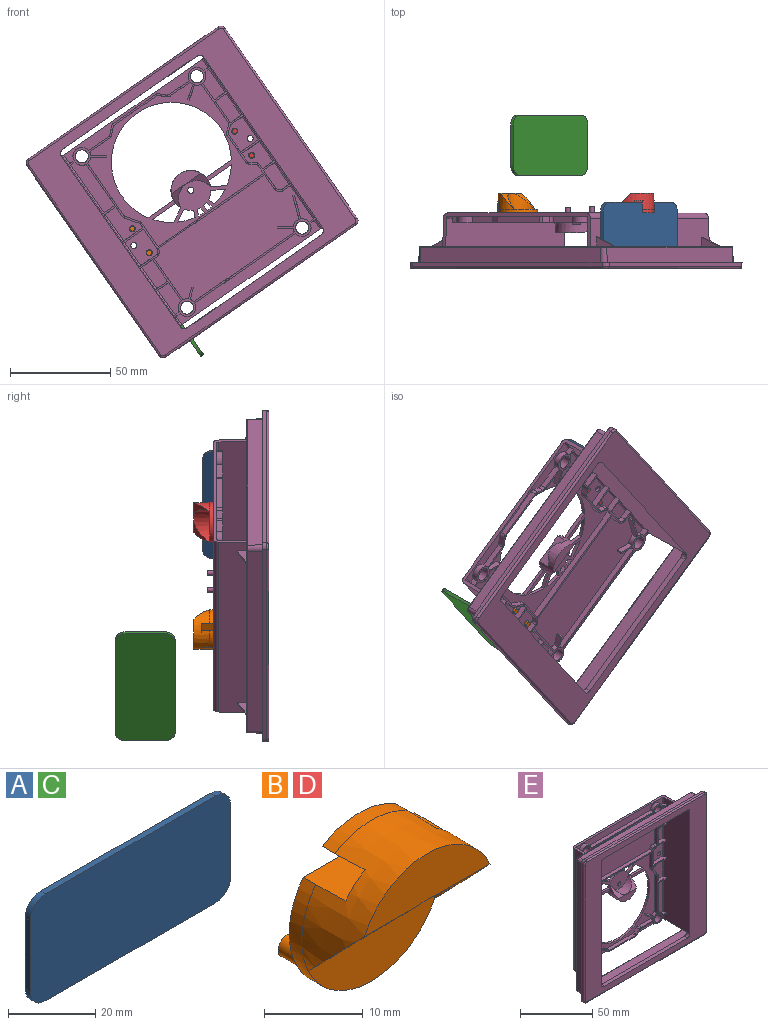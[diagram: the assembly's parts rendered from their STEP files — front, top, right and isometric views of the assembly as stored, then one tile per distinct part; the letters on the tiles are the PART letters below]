
ASSEMBLY  parts=5 mates=5
PART A: 10 faces, bbox 65x1.6x30 mm
  f0: plane 20x1.6mm, normal (1,0,0), area 32mm2, adj f1,f7,f8,f9
  f1: cylinder r=5mm len=5mm, axis (0,1,0), area 12.6mm2, adj f0,f2,f8,f9
  f2: plane 55x1.6mm, normal (0,0,1), area 88mm2, adj f1,f3,f8,f9
  f3: cylinder r=5mm len=5mm, axis (0,1,0), area 12.6mm2, adj f2,f4,f8,f9
  f4: plane 20x1.6mm, normal (-1,0,0), area 32mm2, adj f3,f5,f8,f9
  f5: cylinder r=5mm len=5mm, axis (0,1,0), area 12.6mm2, adj f4,f6,f8,f9
  f6: plane 55x1.6mm, normal (0,0,-1), area 88mm2, adj f5,f7,f8,f9
  f7: cylinder r=5mm len=5mm, axis (0,1,0), area 12.6mm2, adj f0,f6,f8,f9
  f8: plane 65x30mm, normal (0,-1,0), area 1928.5mm2, adj f0,f1,f2,f3,f4,f5,f6,f7
  f9: plane 65x30mm, normal (0,1,0), area 1928.5mm2, adj f0,f1,f2,f3,f4,f5,f6,f7
PART B: 18 faces, bbox 20x12.8x20 mm
  f0: plane 20x16mm, normal (0,1,0), area 252.1mm2, adj f4,f6,f7,f9,f14
  f1: plane 10.54x1.5mm, normal (0,1,0), area 10.7mm2, adj f5,f13
  f2: cone r=10mm half-angle=1deg, axis (0,1,0), area 219.9mm2, adj f4,f5,f12,f13,f14,f15,f16,f17
  f3: plane 18.1x14mm, normal (0,-1,0), area 181.7mm2, adj f4,f6,f11
  f4: cylinder r=10mm len=20mm, axis (0,-1,0), area 79.7mm2, adj f0,f2,f3,f14
  f5: cylinder r=10mm len=10.54mm, axis (0,-1,0), area 20mm2, adj f1,f2,f13
  f6: cylinder r=1.55mm len=3.1mm, axis (0,-1,0), area 17.5mm2, adj f0,f3
  f7: cylinder r=1.25mm len=3mm, axis (0,-1,0), area 23.6mm2, adj f0,f8
  f8: plane 2.5x2.5mm, normal (0,1,0), area 4.9mm2, adj f7
  f9: cylinder r=1.25mm len=3mm, axis (0,-1,0), area 23.6mm2, adj f0,f10
  f10: plane 2.5x2.5mm, normal (0,1,0), area 4.9mm2, adj f9
  f11: cone r=9.09mm half-angle=1deg, axis (0,-1,0), area 139.7mm2, adj f3,f12,f16,f17
  f12: plane 17.99x5.83mm, normal (0,-1,0), area 75.2mm2, adj f2,f11,f16,f17
  f13: plane 10.54x6mm, normal (0,0,-1), area 62.6mm2, adj f1,f2,f5,f15
  f14: plane 16x6mm, normal (0,0,1), area 95.6mm2, adj f0,f2,f4,f15
  f15: plane 15.82x2.5mm, normal (0,1,0), area 33.5mm2, adj f2,f13,f14
  f16: plane 8.54x8.28mm, normal (0,-0.72,-0.69), area 29.8mm2, adj f2,f11,f12
  f17: plane 8.54x8.28mm, normal (0,-0.72,-0.69), area 29.8mm2, adj f2,f11,f12
PART C: same geometry as A
PART D: same geometry as B
PART E: 328 faces, bbox 124.3x34.2x124.3 mm
  f0: cylinder r=30mm len=8.39mm, axis (0,-1,0), area 16.1mm2, adj f97,f100,f298,f317
  f1: cylinder r=30mm len=3.26mm, axis (0,-1,0), area 5.9mm2, adj f97,f100,f299,f301
  f2: cylinder r=30mm len=3.26mm, axis (0,-1,0), area 5.9mm2, adj f97,f100,f302,f304
  f3: cylinder r=30mm len=8.39mm, axis (0,-1,0), area 16.1mm2, adj f97,f100,f305,f307
  f4: cylinder r=30mm len=7.85mm, axis (0,-1,0), area 19.4mm2, adj f97,f100,f308,f310
  f5: cylinder r=30mm len=60mm, axis (0,-1,0), area 230.4mm2, adj f97,f100,f311,f312
  f6: cylinder r=30mm len=7.85mm, axis (0,-1,0), area 19.4mm2, adj f97,f100,f313,f315
  f7: plane 68x2.3mm, normal (0,1,0), area 156.4mm2, adj f16,f227,f239,f240
  f8: plane 21.25x2.3mm, normal (0,1,0), area 48.9mm2, adj f9,f16,f237,f238
  f9: plane 12.94x10.62mm, normal (0,0.01,-1), area 98.4mm2, adj f8,f16,f18,f230,f237,f241,f242,f281
  f10: plane 90.76x6.61mm, normal (0,1,0), area 599mm2, adj f13,f19,f224,f235,f285,f291
  f11: plane 68x2.3mm, normal (0,1,0), area 156.4mm2, adj f12,f224,f233,f234
  f12: plane 104x22.15mm, normal (1,0.02,0), area 2259.9mm2, adj f11,f13,f15,f20,f61,f99,f102,f103
  f13: plane 12.94x10.62mm, normal (0,0.01,1), area 98.4mm2, adj f10,f12,f20,f222,f231,f235,f236,f291
  f14: plane 7.72x7.51mm, normal (1,0.02,0), area 57.6mm2, adj f15,f87,f274,f283
  f15: plane 111.01x8.88mm, normal (0,1,0), area 303.6mm2, adj f12,f14,f16,f72,f73,f74,f86,f87
  f16: plane 104x22.15mm, normal (-1,0.02,0), area 2259.9mm2, adj f7,f8,f9,f15,f61,f101,f102,f103
  f17: plane 89.95x7.51mm, normal (1,0.02,0), area 674.8mm2, adj f18,f275,f279,f281
  f18: plane 90.76x6.61mm, normal (0,1,0), area 599mm2, adj f9,f17,f227,f241,f279,f281
  f19: plane 89.95x7.51mm, normal (-1,0.02,0), area 674.8mm2, adj f10,f276,f285,f291
  f20: plane 21.25x2.3mm, normal (0,1,0), area 48.9mm2, adj f12,f13,f231,f232
  f21: plane 7.72x7.51mm, normal (-1,0.02,0), area 57.6mm2, adj f61,f91,f266,f289
  f22: cone r=4.45mm half-angle=0.5deg, axis (0,1,0), area 10.2mm2, adj f97,f109,f148,f200
  f23: cone r=4.45mm half-angle=0.5deg, axis (0,1,0), area 10.2mm2, adj f97,f109,f146,f161
  f24: plane 104.01x25.12mm, normal (-1,-0.02,0), area 2592mm2, adj f25,f26,f27,f28,f55,f57,f63,f72
  f25: cylinder r=0.9mm len=15.12mm, axis (0,0,-1), area 21.1mm2, adj f24,f36,f140,f164
  f26: cylinder r=0.9mm len=13.12mm, axis (0,0,-1), area 18.3mm2, adj f24,f37,f163,f166
  f27: cylinder r=0.9mm len=14.12mm, axis (0,0,-1), area 19.7mm2, adj f24,f38,f167,f170
  f28: cylinder r=0.9mm len=16.12mm, axis (0,0,-1), area 22.5mm2, adj f24,f43,f169,f189
  f29: cylinder r=0.9mm len=13.12mm, axis (0,0,-1), area 18.3mm2, adj f41,f75,f191,f196
  f30: cylinder r=0.9mm len=14.12mm, axis (0,0,-1), area 19.7mm2, adj f42,f75,f190,f194
  f31: cylinder r=0.9mm len=14.12mm, axis (0,0,-1), area 19.7mm2, adj f40,f75,f144,f197
  f32: cylinder r=0.9mm len=12.12mm, axis (0,0,-1), area 16.9mm2, adj f44,f75,f193,f216
  f33: cylinder r=0.9mm len=13.12mm, axis (0,0,-1), area 18.3mm2, adj f34,f75,f215,f218
  f34: plane 13.1x6.56mm, normal (0,-1,0), area 84.6mm2, adj f33,f156,f215,f218,f219
  f35: plane 76.56x31.95mm, normal (0,-1,0), area 2286.4mm2, adj f45,f46,f58,f59,f60,f108,f131,f132
  f36: plane 15.1x6.56mm, normal (0,-1,0), area 87.3mm2, adj f25,f110,f140,f164,f186
  f37: plane 13.1x6.56mm, normal (0,-1,0), area 86mm2, adj f26,f163,f165,f166
  f38: plane 14.1x11.65mm, normal (0,-1,0), area 147.9mm2, adj f27,f167,f170,f175,f182,f184,f243,f248
  f39: plane 29.1x6.56mm, normal (0,-1,0), area 179.2mm2, adj f51,f55,f141,f160,f188
  f40: plane 14.1x6.56mm, normal (0,-1,0), area 80.8mm2, adj f31,f50,f144,f197,f199
  f41: plane 13.1x6.62mm, normal (0,-1,0), area 86mm2, adj f29,f191,f196,f198,f202
  f42: plane 14.1x10.61mm, normal (0,-1,0), area 129.9mm2, adj f30,f190,f192,f194,f204,f205,f213,f245
  f43: plane 16.1x11.65mm, normal (0,-1,0), area 129.4mm2, adj f28,f162,f169,f171,f176,f178,f181,f189
  f44: plane 12.1x10.61mm, normal (0,-1,0), area 100.4mm2, adj f32,f159,f193,f195,f207,f209,f212,f216
  f45: cone r=4.45mm half-angle=0.5deg, axis (0,1,0), area 9mm2, adj f35,f109,f153,f187
  f46: cone r=4.45mm half-angle=0.5deg, axis (0,1,0), area 6.7mm2, adj f35,f109,f152,f154
  f47: plane 84.02x5.15mm, normal (0,-1,0), area 378.4mm2, adj f48,f49,f57,f96,f102,f138,f139,f151
  f48: cone r=4.45mm half-angle=0.5deg, axis (0,1,0), area 39.2mm2, adj f47,f109,f138,f151
  f49: cone r=4.45mm half-angle=0.5deg, axis (0,1,0), area 39.2mm2, adj f47,f109,f139,f151
  f50: cone r=4.45mm half-angle=0.5deg, axis (0,1,0), area 18.3mm2, adj f40,f109,f144,f199
  f51: cone r=4.45mm half-angle=0.5deg, axis (0,1,0), area 18.3mm2, adj f39,f109,f141,f160
  f52: plane 84.02x5.15mm, normal (0,-1,0), area 252.6mm2, adj f53,f54,f98,f103,f111,f113,f116,f118
  f53: cylinder r=0.9mm len=5.17mm, axis (0,0,-1), area 7.2mm2, adj f52,f75,f103,f143
  f54: cone r=4.45mm half-angle=0.5deg, axis (0,1,0), area 39.2mm2, adj f52,f109,f116,f143
  f55: cylinder r=0.9mm len=29.12mm, axis (0,0,-1), area 40.7mm2, adj f24,f39,f141,f188
  f56: cone r=4.45mm half-angle=0.5deg, axis (0,1,0), area 5.5mm2, adj f97,f109,f114,f145
  f57: cylinder r=0.9mm len=5.17mm, axis (0,0,-1), area 7.2mm2, adj f24,f47,f102,f139
  f58: cylinder r=0.9mm len=20.12mm, axis (0,0,-1), area 28.1mm2, adj f35,f75,f137,f217
  f59: cone r=4.45mm half-angle=0.5deg, axis (0,1,0), area 13.6mm2, adj f35,f109,f135,f137
  f60: cone r=4.45mm half-angle=0.5deg, axis (0,1,0), area 14.8mm2, adj f35,f109,f132,f134
  f61: plane 111.01x8.88mm, normal (0,1,0), area 303.6mm2, adj f12,f16,f21,f76,f77,f78,f88,f89
  f62: plane 120.5x120.5mm, normal (0,1,0), area 1523.2mm2, adj f64,f65,f66,f67,f68,f69,f70,f71
  f63: plane 118.5x118.5mm, normal (0,-1,0), area 4621.4mm2, adj f24,f72,f73,f74,f75,f76,f77,f78
  f64: plane 115.5x2mm, normal (1,0,0), area 231mm2, adj f62,f65,f71,f252
  f65: cylinder r=2.5mm len=2.5mm, axis (0,-1,0), area 7.9mm2, adj f62,f64,f66,f254
  f66: plane 115.5x2mm, normal (0,0,1), area 231mm2, adj f62,f65,f67,f256
  f67: cylinder r=2.5mm len=2.5mm, axis (0,-1,0), area 7.9mm2, adj f62,f66,f68,f255
  f68: plane 115.5x2mm, normal (-1,0,0), area 231mm2, adj f62,f67,f69,f253
  f69: cylinder r=2.5mm len=2.5mm, axis (0,-1,0), area 7.9mm2, adj f62,f68,f70,f251
  f70: plane 115.5x2mm, normal (0,0,-1), area 231mm2, adj f62,f69,f71,f249
  f71: cylinder r=2.5mm len=2.5mm, axis (0,-1,0), area 7.9mm2, adj f62,f64,f70,f250
  f72: cone r=2.5mm half-angle=1deg, axis (0,-1,0), area 11.7mm2, adj f15,f24,f63,f73
  f73: plane 81.7x3mm, normal (0,-0.02,-1), area 245.1mm2, adj f15,f63,f72,f74
  f74: cone r=2.5mm half-angle=1deg, axis (0,-1,0), area 11.7mm2, adj f15,f63,f73,f75
  f75: plane 104.01x25.12mm, normal (1,-0.02,0), area 2590.1mm2, adj f29,f30,f31,f32,f33,f53,f58,f63
  f76: cone r=2.5mm half-angle=1deg, axis (0,-1,0), area 11.7mm2, adj f61,f63,f75,f77
  f77: plane 81.7x3mm, normal (0,-0.02,1), area 245.1mm2, adj f61,f63,f76,f78
  f78: cone r=2.5mm half-angle=1deg, axis (0,-1,0), area 11.7mm2, adj f24,f61,f63,f77
  f79: plane 109.5x7.51mm, normal (0,0.02,-1), area 822.3mm2, adj f62,f80,f94,f264
  f80: cone r=2.25mm half-angle=1deg, axis (0,-1,0), area 25.8mm2, adj f62,f79,f81,f262
  f81: plane 109.5x7.51mm, normal (-1,0.02,0), area 822.3mm2, adj f62,f80,f82,f260
  f82: cone r=2.25mm half-angle=1deg, axis (0,-1,0), area 25.8mm2, adj f62,f81,f83,f258
  f83: plane 109.5x7.51mm, normal (0,0.02,1), area 822.3mm2, adj f62,f82,f84,f257
  f84: cone r=2.25mm half-angle=1deg, axis (0,-1,0), area 25.8mm2, adj f62,f83,f85,f259
  f85: plane 109.5x7.51mm, normal (1,0.02,0), area 822.3mm2, adj f62,f84,f94,f261
  f86: plane 109.5x7.51mm, normal (0,0.02,-1), area 822.3mm2, adj f15,f87,f93,f272
  f87: cone r=0.75mm half-angle=1deg, axis (0,1,0), area 9.6mm2, adj f14,f15,f86,f273
  f88: plane 7.72x7.51mm, normal (1,0.02,0), area 57.6mm2, adj f61,f89,f265,f277
  f89: cone r=0.75mm half-angle=1deg, axis (0,1,0), area 9.6mm2, adj f61,f88,f90,f267
  f90: plane 109.5x7.51mm, normal (0,0.02,1), area 822.3mm2, adj f61,f89,f91,f269
  f91: cone r=0.75mm half-angle=1deg, axis (0,1,0), area 9.6mm2, adj f21,f61,f90,f268
  f92: plane 7.72x7.51mm, normal (-1,0.02,0), area 57.6mm2, adj f15,f93,f270,f287
  f93: cone r=0.75mm half-angle=1deg, axis (0,1,0), area 9.6mm2, adj f15,f86,f92,f271
  f94: cone r=2.25mm half-angle=1deg, axis (0,-1,0), area 25.8mm2, adj f62,f79,f85,f263
  f95: plane 112.79x112.79mm, normal (0,1,0), area 109.6mm2, adj f222,f225,f228,f230,f257,f258,f259,f260
  f96: cylinder r=0.9mm len=5.17mm, axis (0,0,-1), area 7.2mm2, adj f47,f75,f102,f138
  f97: plane 69.1x62.25mm, normal (0,-1,0), area 1388.1mm2, adj f0,f1,f2,f3,f4,f5,f6,f22
  f98: cylinder r=0.9mm len=5.17mm, axis (0,0,-1), area 7.2mm2, adj f24,f52,f103,f142
  f99: cylinder r=2.7mm len=103.23mm, axis (0,0,-1), area 432.7mm2, adj f12,f100,f102,f103
  f100: plane 103.13x84.02mm, normal (0,1,0), area 6018.9mm2, adj f0,f1,f2,f3,f4,f5,f6,f99
  f101: cylinder r=2.7mm len=103.23mm, axis (0,0,-1), area 432.7mm2, adj f16,f100,f102,f103
  f102: plane 90.22x24.82mm, normal (0,0.02,1), area 241.1mm2, adj f12,f15,f16,f24,f47,f57,f75,f96
  f103: plane 90.22x24.82mm, normal (0,0.02,-1), area 241mm2, adj f12,f16,f24,f52,f53,f61,f75,f98
  f104: cylinder r=3.25mm len=6.5mm, axis (0,-1,0), area 98mm2, adj f100,f109
  f105: cylinder r=3.25mm len=6.5mm, axis (0,-1,0), area 98mm2, adj f100,f109
  f106: cylinder r=3.25mm len=6.5mm, axis (0,-1,0), area 98mm2, adj f100,f109
  f107: cylinder r=3.25mm len=6.5mm, axis (0,-1,0), area 98mm2, adj f100,f109
  f108: cone r=4.45mm half-angle=0.5deg, axis (0,1,0), area 5.5mm2, adj f35,f109,f131,f152
  f109: plane 100.85x85.9mm, normal (0,-1,0), area 520.3mm2, adj f22,f23,f24,f45,f46,f48,f49,f50
  f110: cone r=4.45mm half-angle=0.5deg, axis (0,1,0), area 18.3mm2, adj f36,f109,f140,f186
  f111: cone r=4.45mm half-angle=0.5deg, axis (0,1,0), area 39.2mm2, adj f52,f109,f113,f142
  f112: cone r=4.45mm half-angle=0.5deg, axis (0,1,0), area 5.5mm2, adj f97,f109,f115,f149
  f113: plane 12.22x3mm, normal (0,-0.01,-1), area 36.6mm2, adj f52,f109,f111,f125
  f114: plane 12.22x3mm, normal (0,-0.01,1), area 36.6mm2, adj f56,f97,f109,f126
  f115: plane 11.8x3mm, normal (0,-0.01,1), area 35.4mm2, adj f97,f109,f112,f130
  f116: plane 11.8x3mm, normal (0,-0.01,-1), area 35.4mm2, adj f52,f54,f109,f129
  f117: plane 3x2.55mm, normal (0.71,-0.01,0.71), area 10.8mm2, adj f97,f109,f127,f130
  f118: plane 3x2.55mm, normal (-0.71,-0.01,-0.71), area 10.8mm2, adj f52,f109,f128,f129
  f119: plane 25.44x3mm, normal (0,-0.01,1), area 76.3mm2, adj f97,f109,f123,f127
  f120: plane 25.44x3mm, normal (0,-0.01,-1), area 76.3mm2, adj f52,f109,f124,f128
  f121: plane 3x2.85mm, normal (-0.71,-0.01,0.71), area 12mm2, adj f97,f109,f123,f126
  f122: plane 3x2.85mm, normal (0.71,-0.01,-0.71), area 12mm2, adj f52,f109,f124,f125
  f123: cone r=1.55mm half-angle=0.5deg, axis (0,-1,0), area 3.7mm2, adj f97,f109,f119,f121
  f124: cone r=2.45mm half-angle=0.5deg, axis (0,1,0), area 5.7mm2, adj f52,f109,f120,f122
  f125: cone r=1.55mm half-angle=0.5deg, axis (0,-1,0), area 3.7mm2, adj f52,f109,f113,f122
  f126: cone r=2.45mm half-angle=0.5deg, axis (0,1,0), area 5.7mm2, adj f97,f109,f114,f121
  f127: cone r=1.55mm half-angle=0.5deg, axis (0,-1,0), area 3.7mm2, adj f97,f109,f117,f119
  f128: cone r=2.45mm half-angle=0.5deg, axis (0,1,0), area 5.7mm2, adj f52,f109,f118,f120
  f129: cone r=2.55mm half-angle=0.5deg, axis (0,-1,0), area 6mm2, adj f52,f109,f116,f118
  f130: cone r=3.45mm half-angle=0.5deg, axis (0,1,0), area 8.1mm2, adj f97,f109,f115,f117
  f131: plane 6.61x4.61mm, normal (0.57,-0.01,0.82), area 24.1mm2, adj f35,f108,f109,f133
  f132: plane 6.58x4.64mm, normal (-0.57,-0.01,-0.82), area 24.1mm2, adj f35,f60,f109,f133
  f133: plane 3x0.74mm, normal (0.82,-0.01,-0.57), area 2.6mm2, adj f35,f109,f131,f132
  f134: plane 11.33x4.13mm, normal (0.94,-0.01,-0.34), area 36.1mm2, adj f35,f60,f109,f136
  f135: plane 11.31x4.14mm, normal (-0.94,-0.01,0.34), area 36.1mm2, adj f35,f59,f109,f136
  f136: plane 3x0.85mm, normal (-0.34,-0.01,-0.94), area 2.6mm2, adj f35,f109,f134,f135
  f137: plane 3.55x3mm, normal (0,-0.01,-1), area 10.4mm2, adj f35,f58,f59,f75,f109
  f138: plane 3.55x3mm, normal (0,-0.01,1), area 10.4mm2, adj f47,f48,f75,f96,f109
  f139: plane 3.55x3mm, normal (0,-0.01,1), area 10.4mm2, adj f24,f47,f49,f57,f109
  f140: plane 3.55x3mm, normal (0,-0.01,-1), area 10.4mm2, adj f24,f25,f36,f109,f110
  f141: plane 3.55x3mm, normal (0,-0.01,1), area 10.4mm2, adj f24,f39,f51,f55,f109
  f142: plane 3.55x3mm, normal (0,-0.01,-1), area 10.4mm2, adj f24,f52,f98,f109,f111
  f143: plane 3.55x3mm, normal (0,-0.01,-1), area 10.4mm2, adj f52,f53,f54,f75,f109
  f144: plane 3.55x3mm, normal (0,-0.01,1), area 10.4mm2, adj f31,f40,f50,f75,f109
  f145: plane 6.61x4.61mm, normal (-0.57,-0.01,-0.82), area 24.1mm2, adj f56,f97,f109,f147
  f146: plane 6.58x4.64mm, normal (0.57,-0.01,0.82), area 24.1mm2, adj f23,f97,f109,f147
  f147: plane 3x0.74mm, normal (-0.82,-0.01,0.57), area 2.6mm2, adj f97,f109,f145,f146
  f148: plane 6.58x4.64mm, normal (-0.57,-0.01,0.82), area 24.1mm2, adj f22,f97,f109,f150
  f149: plane 6.61x4.61mm, normal (0.57,-0.01,-0.82), area 24.1mm2, adj f97,f109,f112,f150
  f150: plane 3x0.74mm, normal (0.82,-0.01,0.57), area 2.6mm2, adj f97,f109,f148,f149
  f151: plane 61.19x3mm, normal (0,-0.01,1), area 183.5mm2, adj f47,f48,f49,f109
  f152: plane 61.19x3mm, normal (0,-0.01,-1), area 183.5mm2, adj f35,f46,f108,f109
  f153: plane 4.62x3.91mm, normal (0.64,-0.01,-0.77), area 18.1mm2, adj f35,f45,f109,f155
  f154: plane 4.65x3.87mm, normal (-0.64,-0.01,0.77), area 18.1mm2, adj f35,f46,f109,f155
  f155: plane 3x0.69mm, normal (-0.77,-0.01,-0.64), area 2.6mm2, adj f35,f109,f153,f154
  f156: plane 10.58x3mm, normal (-1,-0.01,0), area 31.7mm2, adj f34,f109,f215,f219
  f157: plane 4.69x3mm, normal (1,-0.01,0), area 14mm2, adj f97,f109,f173,f211
  f158: plane 8.43x3mm, normal (1,-0.01,0), area 25.2mm2, adj f35,f109,f172,f220
  f159: plane 3x2.54mm, normal (-1,-0.01,0), area 7.6mm2, adj f44,f109,f212,f216
  f160: plane 25.17x3mm, normal (1,-0.01,0), area 75.4mm2, adj f39,f51,f109,f188
  f161: plane 31.7x3mm, normal (-1,-0.01,0), area 95.1mm2, adj f23,f97,f109,f180
  f162: plane 5.68x3mm, normal (1,-0.01,0), area 17mm2, adj f43,f109,f181,f189
  f163: plane 7.53x3mm, normal (0,-0.01,-1), area 22.3mm2, adj f24,f26,f37,f109,f165
  f164: plane 7.53x3mm, normal (0,-0.01,1), area 22.3mm2, adj f24,f25,f36,f109,f186
  f165: plane 13.15x3mm, normal (1,-0.01,0), area 39.4mm2, adj f37,f109,f163,f166
  f166: plane 7.53x3mm, normal (0,-0.01,1), area 22.3mm2, adj f24,f26,f37,f109,f165
  f167: plane 10.37x3mm, normal (0,-0.01,-1), area 30.9mm2, adj f24,f27,f38,f109,f182
  f168: plane 3x2mm, normal (0,-0.01,1), area 5.9mm2, adj f35,f109,f183,f187
  f169: plane 12.62x3mm, normal (0,-0.01,-1), area 37.6mm2, adj f24,f28,f43,f109,f171
  f170: plane 12.62x3mm, normal (0,-0.01,1), area 37.6mm2, adj f24,f27,f38,f109,f175
  f171: plane 3x1.95mm, normal (1,-0.01,0), area 5.8mm2, adj f43,f109,f169,f178
  f172: plane 64.23x3mm, normal (0,-0.01,1), area 192.6mm2, adj f35,f109,f158,f185
  f173: plane 64.06x3mm, normal (0,-0.01,-1), area 192.1mm2, adj f97,f109,f157,f174
  f174: plane 14.1x3mm, normal (-1,-0.01,0), area 42.2mm2, adj f97,f109,f173,f179
  f175: plane 11.63x3mm, normal (1,-0.01,0), area 34.8mm2, adj f38,f109,f170,f184
  f176: plane 6.25x4.39mm, normal (0.82,-0.01,0.57), area 22.8mm2, adj f43,f109,f178,f181
  f177: plane 6.25x4.39mm, normal (-0.82,-0.01,-0.57), area 22.8mm2, adj f97,f109,f179,f180
  f178: cone r=1.55mm half-angle=0.5deg, axis (0,-1,0), area 2.9mm2, adj f43,f109,f171,f176
  f179: cone r=2.45mm half-angle=0.5deg, axis (0,1,0), area 4.5mm2, adj f97,f109,f174,f177
  f180: cone r=1.55mm half-angle=0.5deg, axis (0,-1,0), area 2.9mm2, adj f97,f109,f161,f177
  f181: cone r=2.45mm half-angle=0.5deg, axis (0,1,0), area 4.5mm2, adj f43,f109,f162,f176
  f182: cone r=1.55mm half-angle=0.5deg, axis (0,-1,0), area 5.2mm2, adj f38,f109,f167,f184
  f183: cone r=2.45mm half-angle=0.5deg, axis (0,1,0), area 8.1mm2, adj f35,f109,f168,f185
  f184: plane 3x1.67mm, normal (0.89,-0.01,-0.45), area 5.6mm2, adj f38,f109,f175,f182
  f185: plane 3x1.53mm, normal (-0.89,-0.01,0.45), area 5.1mm2, adj f35,f109,f172,f183
  f186: plane 11.17x3mm, normal (1,-0.01,0), area 33.4mm2, adj f36,f109,f110,f164
  f187: plane 25.17x3mm, normal (-1,-0.01,0), area 75.4mm2, adj f35,f45,f109,f168
  f188: plane 7.53x3mm, normal (0,-0.01,-1), area 22.3mm2, adj f24,f39,f55,f109,f160
  f189: plane 7.53x3mm, normal (0,-0.01,1), area 22.3mm2, adj f24,f28,f43,f109,f162
  f190: plane 7.99x3mm, normal (0,-0.01,1), area 23.7mm2, adj f30,f42,f75,f109,f192
  f191: plane 7.6x3mm, normal (0,-0.01,-1), area 22.5mm2, adj f29,f41,f75,f109,f202
  f192: cone r=2.45mm half-angle=0.5deg, axis (0,1,0), area 2.4mm2, adj f42,f109,f190,f204
  f193: plane 11.58x3mm, normal (0,-0.01,1), area 34.4mm2, adj f32,f44,f75,f109,f195
  f194: plane 11.58x3mm, normal (0,-0.01,-1), area 34.4mm2, adj f30,f42,f75,f109,f205
  f195: plane 4.7x3mm, normal (-1,-0.01,0), area 14.1mm2, adj f44,f109,f193,f209
  f196: plane 7.53x3mm, normal (0,-0.01,1), area 22.3mm2, adj f29,f41,f75,f109,f198
  f197: plane 7.53x3mm, normal (0,-0.01,-1), area 22.3mm2, adj f31,f40,f75,f109,f199
  f198: plane 12.58x3mm, normal (-1,-0.01,0), area 37.7mm2, adj f41,f109,f196,f202
  f199: plane 10.17x3mm, normal (-1,-0.01,0), area 30.4mm2, adj f40,f50,f109,f197
  f200: plane 23.6x3mm, normal (1,-0.01,0), area 70.8mm2, adj f22,f97,f109,f201
  f201: cone r=1.55mm half-angle=0.5deg, axis (0,-1,0), area 4.5mm2, adj f97,f109,f200,f203
  f202: cone r=2.45mm half-angle=0.5deg, axis (0,1,0), area 1.7mm2, adj f41,f109,f191,f198
  f203: plane 3x2.36mm, normal (0.57,-0.01,-0.82), area 8.6mm2, adj f97,f109,f201,f214
  f204: plane 3x2.36mm, normal (-0.57,-0.01,0.82), area 8.6mm2, adj f42,f109,f192,f213
  f205: plane 10.66x3mm, normal (-1,-0.01,0), area 31.9mm2, adj f42,f109,f194,f213
  f206: plane 16.2x3mm, normal (1,-0.01,0), area 48.6mm2, adj f97,f109,f210,f214
  f207: plane 3x2.36mm, normal (-0.57,-0.01,-0.82), area 8.6mm2, adj f44,f109,f209,f212
  f208: plane 3x2.36mm, normal (0.57,-0.01,0.82), area 8.6mm2, adj f97,f109,f210,f211
  f209: cone r=1.55mm half-angle=0.5deg, axis (0,-1,0), area 4.5mm2, adj f44,f109,f195,f207
  f210: cone r=2.45mm half-angle=0.5deg, axis (0,1,0), area 7mm2, adj f97,f109,f206,f208
  f211: cone r=1.55mm half-angle=0.5deg, axis (0,-1,0), area 4.5mm2, adj f97,f109,f157,f208
  f212: cone r=2.45mm half-angle=0.5deg, axis (0,1,0), area 7mm2, adj f44,f109,f159,f207
  f213: cone r=1.55mm half-angle=0.5deg, axis (0,-1,0), area 4.5mm2, adj f42,f109,f204,f205
  f214: cone r=2.45mm half-angle=0.5deg, axis (0,1,0), area 7mm2, adj f97,f109,f203,f206
  f215: plane 7.53x3mm, normal (0,-0.01,1), area 22.3mm2, adj f33,f34,f75,f109,f156
  f216: plane 7.53x3mm, normal (0,-0.01,-1), area 22.3mm2, adj f32,f44,f75,f109,f159
  f217: plane 4.95x3mm, normal (0,-0.01,1), area 14.6mm2, adj f35,f58,f75,f109,f220
  f218: plane 4.95x3mm, normal (0,-0.01,-1), area 14.6mm2, adj f33,f34,f75,f109,f219
  f219: cone r=2.55mm half-angle=0.5deg, axis (0,-1,0), area 12.1mm2, adj f34,f109,f156,f218
  f220: cone r=3.45mm half-angle=0.5deg, axis (0,1,0), area 16.2mm2, adj f35,f109,f158,f217
  f221: plane 12.94x10.62mm, normal (0,0.01,-1), area 105.9mm2, adj f12,f61,f222,f289,f290
  f222: plane 10.78x4.81mm, normal (0.41,0.91,0), area 11.5mm2, adj f12,f13,f95,f221,f290,f292
  f223: plane 12.94x10.62mm, normal (0,0.01,1), area 105.9mm2, adj f12,f15,f225,f287,f288
  f224: plane 12.94x10.62mm, normal (0,0.01,-1), area 98.4mm2, adj f10,f11,f12,f225,f234,f235,f236,f285
  f225: plane 10.78x4.81mm, normal (0.41,0.91,0), area 11.5mm2, adj f12,f95,f223,f224,f286,f288
  f226: plane 12.94x10.62mm, normal (0,0.01,-1), area 105.9mm2, adj f16,f61,f228,f277,f278
  f227: plane 12.94x10.62mm, normal (0,0.01,1), area 98.4mm2, adj f7,f16,f18,f228,f240,f241,f242,f279
  f228: plane 10.78x4.81mm, normal (-0.41,0.91,0), area 11.5mm2, adj f16,f95,f226,f227,f278,f280
  f229: plane 12.94x10.62mm, normal (0,0.01,1), area 105.9mm2, adj f15,f16,f230,f283,f284
  f230: plane 10.78x4.81mm, normal (-0.41,0.91,0), area 11.5mm2, adj f9,f16,f95,f229,f282,f284
  f231: plane 21.32x5mm, normal (-1,0,0), area 106.4mm2, adj f13,f20,f232,f236
  f232: plane 5x2.39mm, normal (0,0,-1), area 11.7mm2, adj f12,f20,f231,f236
  f233: plane 5x2.39mm, normal (0,0,1), area 11.7mm2, adj f11,f12,f234,f236
  f234: plane 68.07x5mm, normal (-1,0,0), area 340.2mm2, adj f11,f224,f233,f236
  f235: plane 90.88x5mm, normal (1,0,0), area 454.1mm2, adj f10,f13,f224,f236
  f236: plane 90.88x3.89mm, normal (0,1,0), area 139.9mm2, adj f12,f13,f224,f231,f232,f233,f234,f235
  f237: plane 21.32x5mm, normal (1,0,0), area 106.4mm2, adj f8,f9,f238,f242
  f238: plane 5x2.39mm, normal (0,0,1), area 11.7mm2, adj f8,f16,f237,f242
  f239: plane 5x2.39mm, normal (0,0,-1), area 11.7mm2, adj f7,f16,f240,f242
  f240: plane 68.07x5mm, normal (1,0,0), area 340.2mm2, adj f7,f227,f239,f242
  f241: plane 90.88x5mm, normal (-1,0,0), area 454.1mm2, adj f9,f18,f227,f242
  f242: plane 90.88x3.89mm, normal (0,1,0), area 139.9mm2, adj f9,f16,f227,f237,f238,f239,f240,f241
  f243: cylinder r=1.5mm len=3mm, axis (0,1,0), area 17mm2, adj f38,f100
  f244: cylinder r=1.5mm len=3mm, axis (0,1,0), area 17mm2, adj f43,f100
  f245: cylinder r=1.55mm len=3.1mm, axis (0,1,0), area 17.5mm2, adj f42,f100
  f246: cylinder r=1.5mm len=3mm, axis (0,1,0), area 17mm2, adj f42,f100
  f247: cylinder r=1.5mm len=3mm, axis (0,1,0), area 17mm2, adj f44,f100
  f248: cylinder r=1.55mm len=3.1mm, axis (0,1,0), area 17.5mm2, adj f38,f100
  f249: cylinder r=1mm len=115.5mm, axis (1,0,0), area 181.4mm2, adj f63,f70,f250,f251
  f250: torus R=1.5mm, axis (0,-1,0), area 5.3mm2, adj f63,f71,f249,f252
  f251: torus R=1.5mm, axis (0,-1,0), area 5.3mm2, adj f63,f69,f249,f253
  f252: cylinder r=1mm len=115.5mm, axis (0,0,1), area 181.4mm2, adj f63,f64,f250,f254
  f253: cylinder r=1mm len=115.5mm, axis (0,0,-1), area 181.4mm2, adj f63,f68,f251,f255
  f254: torus R=1.5mm, axis (0,-1,0), area 5.3mm2, adj f63,f65,f252,f256
  f255: torus R=1.5mm, axis (0,-1,0), area 5.3mm2, adj f63,f67,f253,f256
  f256: cylinder r=1mm len=115.5mm, axis (-1,0,0), area 181.4mm2, adj f63,f66,f254,f255
  f257: cylinder r=0.5mm len=109.5mm, axis (1,0,0), area 85mm2, adj f83,f95,f258,f259
  f258: torus R=1.62mm, axis (0,1,0), area 2.4mm2, adj f82,f95,f257,f260
  f259: torus R=1.62mm, axis (0,1,0), area 2.4mm2, adj f84,f95,f257,f261
  f260: cylinder r=0.5mm len=109.5mm, axis (0,0,-1), area 85mm2, adj f81,f95,f258,f262
  f261: cylinder r=0.5mm len=109.5mm, axis (0,0,-1), area 85mm2, adj f85,f95,f259,f263
  f262: torus R=1.62mm, axis (0,1,0), area 2.4mm2, adj f80,f95,f260,f264
  f263: torus R=1.62mm, axis (0,1,0), area 2.4mm2, adj f94,f95,f261,f264
  f264: cylinder r=0.5mm len=109.5mm, axis (1,0,0), area 85mm2, adj f79,f95,f262,f263
  f265: cylinder r=0.5mm len=7.74mm, axis (0,0,-1), area 6mm2, adj f88,f95,f267,f278
  f266: cylinder r=0.5mm len=7.74mm, axis (0,0,-1), area 6mm2, adj f21,f95,f268,f290
  f267: torus R=1.38mm, axis (0,1,0), area 1.3mm2, adj f89,f95,f265,f269
  f268: torus R=1.38mm, axis (0,1,0), area 1.3mm2, adj f91,f95,f266,f269
  f269: cylinder r=0.5mm len=109.5mm, axis (1,0,0), area 85mm2, adj f90,f95,f267,f268
  f270: cylinder r=0.5mm len=7.74mm, axis (0,0,-1), area 6mm2, adj f92,f95,f271,f288
  f271: torus R=1.38mm, axis (0,1,0), area 1.3mm2, adj f93,f95,f270,f272
  f272: cylinder r=0.5mm len=109.5mm, axis (1,0,0), area 85mm2, adj f86,f95,f271,f273
  f273: torus R=1.38mm, axis (0,1,0), area 1.3mm2, adj f87,f95,f272,f274
  f274: cylinder r=0.5mm len=7.74mm, axis (0,0,-1), area 6mm2, adj f14,f95,f273,f284
  f275: cylinder r=0.5mm len=89.97mm, axis (0,0,-1), area 69.9mm2, adj f17,f95,f280,f282
  f276: cylinder r=0.5mm len=89.97mm, axis (0,0,-1), area 69.9mm2, adj f19,f95,f286,f292
  f277: cylinder r=0.5mm len=7.52mm, axis (-0.02,1,0.01), area 5.9mm2, adj f61,f88,f226,f278
  f278: bspline ~1.17x1.04mm, area 0.5mm2, adj f95,f226,f228,f265,f277
  f279: cylinder r=0.5mm len=7.52mm, axis (-0.02,1,-0.01), area 5.9mm2, adj f17,f18,f227,f280
  f280: bspline ~1.04x1mm, area 0.5mm2, adj f95,f227,f228,f275,f279
  f281: cylinder r=0.5mm len=7.52mm, axis (-0.02,1,0.01), area 5.9mm2, adj f9,f17,f18,f282
  f282: bspline ~1.17x1.04mm, area 0.5mm2, adj f9,f95,f230,f275,f281
  f283: cylinder r=0.5mm len=7.52mm, axis (-0.02,1,-0.01), area 5.9mm2, adj f14,f15,f229,f284
  f284: bspline ~1.04x1mm, area 0.5mm2, adj f95,f229,f230,f274,f283
  f285: cylinder r=0.5mm len=7.52mm, axis (-0.02,-1,-0.01), area 5.9mm2, adj f10,f19,f224,f286
  f286: bspline ~1.04x1.04mm, area 0.5mm2, adj f95,f224,f225,f276,f285
  f287: cylinder r=0.5mm len=7.52mm, axis (-0.02,-1,0.01), area 5.9mm2, adj f15,f92,f223,f288
  f288: bspline ~1.04x1mm, area 0.5mm2, adj f95,f223,f225,f270,f287
  f289: cylinder r=0.5mm len=7.52mm, axis (-0.02,-1,-0.01), area 5.9mm2, adj f21,f61,f221,f290
  f290: bspline ~1.04x1.04mm, area 0.5mm2, adj f95,f221,f222,f266,f289
  f291: cylinder r=0.5mm len=7.52mm, axis (-0.02,-1,0.01), area 5.9mm2, adj f10,f13,f19,f292
  f292: bspline ~1.04x1mm, area 0.5mm2, adj f13,f95,f222,f276,f291
  f293: cone r=10mm half-angle=1deg, axis (0,1,0), area 191.8mm2, adj f97,f294,f295,f309,f314,f322,f323,f324
  f294: cylinder r=10mm len=5.03mm, axis (0,-1,0), area 9.8mm2, adj f100,f293,f312,f327
  f295: cylinder r=10mm len=5.03mm, axis (0,-1,0), area 9.8mm2, adj f100,f293,f311,f327
  f296: cone r=9.09mm half-angle=1deg, axis (0,-1,0), area 108.1mm2, adj f97,f323,f324
  f297: cylinder r=10mm len=3.61mm, axis (0,-1,0), area 8.7mm2, adj f97,f100,f298,f317
  f298: plane 3.5x1.8mm, normal (0.93,0,-0.37), area 6.8mm2, adj f0,f97,f100,f297
  f299: plane 3.14x1.8mm, normal (-0.93,0,0.37), area 6.1mm2, adj f1,f97,f100,f300
  f300: cylinder r=10mm len=2mm, axis (0,-1,0), area 3.7mm2, adj f97,f100,f299,f301
  f301: plane 3.03x1.8mm, normal (1,0,0), area 5.4mm2, adj f1,f97,f100,f300
  f302: plane 3.03x1.8mm, normal (-1,0,0), area 5.4mm2, adj f2,f97,f100,f303
  f303: cylinder r=10mm len=2mm, axis (0,-1,0), area 3.7mm2, adj f97,f100,f302,f304
  f304: plane 3.14x1.8mm, normal (0.93,0,0.37), area 6.1mm2, adj f2,f97,f100,f303
  f305: plane 3.5x1.8mm, normal (-0.93,0,-0.37), area 6.8mm2, adj f3,f97,f100,f306
  f306: cylinder r=10mm len=3.61mm, axis (0,-1,0), area 8.7mm2, adj f97,f100,f305,f307
  f307: plane 6.19x3.58mm, normal (0.5,0,0.87), area 12.9mm2, adj f3,f97,f100,f306
  f308: plane 7.07x4.08mm, normal (-0.5,0,-0.87), area 14.7mm2, adj f4,f97,f100,f309
  f309: cylinder r=10mm len=3.2mm, axis (0,-1,0), area 6mm2, adj f100,f293,f308,f310
  f310: plane 14.05x1.8mm, normal (0,0,1), area 25.3mm2, adj f4,f97,f100,f309
  f311: plane 15.43x1.8mm, normal (0,0,-1), area 27.8mm2, adj f5,f97,f100,f295
  f312: plane 15.43x1.8mm, normal (0,0,-1), area 27.8mm2, adj f5,f97,f100,f294
  f313: plane 14.05x1.8mm, normal (0,0,1), area 25.3mm2, adj f6,f97,f100,f314
  f314: cylinder r=10mm len=3.2mm, axis (0,-1,0), area 6mm2, adj f100,f293,f313,f315
  f315: plane 7.07x4.08mm, normal (0.5,0,-0.87), area 14.7mm2, adj f6,f97,f100,f314
  f316: cylinder r=1.55mm len=3.1mm, axis (0,-1,0), area 17.5mm2, adj f97,f100
  f317: plane 6.19x3.58mm, normal (-0.5,0,0.87), area 12.9mm2, adj f0,f97,f100,f297
  f318: cylinder r=1.25mm len=3mm, axis (0,-1,0), area 23.6mm2, adj f100,f319
  f319: plane 2.5x2.5mm, normal (0,1,0), area 4.9mm2, adj f318
  f320: cylinder r=1.25mm len=3mm, axis (0,-1,0), area 23.6mm2, adj f100,f321
  f321: plane 2.5x2.5mm, normal (0,1,0), area 4.9mm2, adj f320
  f322: plane 17.9x5.72mm, normal (0,-1,0), area 73.6mm2, adj f293,f323,f324
  f323: plane 13.36x11.82mm, normal (0,-0.72,0.69), area 30.8mm2, adj f293,f296,f322
  f324: plane 13.36x11.82mm, normal (0,-0.72,0.69), area 30.8mm2, adj f293,f296,f322
  f325: plane 15.66x2mm, normal (0,1,0), area 27.5mm2, adj f293,f326,f327
  f326: plane 11.46x2.22mm, normal (0,0.64,0.77), area 22.6mm2, adj f293,f325
  f327: plane 16x6mm, normal (0,0.02,-1), area 95.2mm2, adj f100,f293,f294,f295,f325
PLACE A rot(axis=(0.35,-0.66,0.66),141.8deg) t=(184.67,228.49,175.43)mm
PLACE B rot(axis=(-0.89,0,0.46),180deg) t=(114.75,266.82,126.14)mm
PLACE C rot(axis=(-0.8,0.42,0.42),102.4deg) t=(121.3,273.73,111.24)mm
PLACE D rot(axis=(0.46,0,0.89),180deg) t=(174.45,266.82,180.75)mm
PLACE E rot(axis=(0,1,0),145.2deg) t=(144.6,211.22,153.45)mm
MATE slider A.f2 <-> E.f7  axis (0,-1,0) through (176.07,214.22,189.19)mm
MATE slider D.f2 <-> E.f245  axis (0,-1,0) through (173.63,239.02,180.18)mm
MATE slider E.f244 <-> B.f9  axis (0,1,0) through (114.85,239.02,135.18)mm
MATE slider B.f2 <-> E.f248  axis (0,-1,0) through (115.57,239.02,126.71)mm
MATE slider D.f7 <-> E.f246  axis (0,-1,0) through (165.94,236.02,183.8)mm
